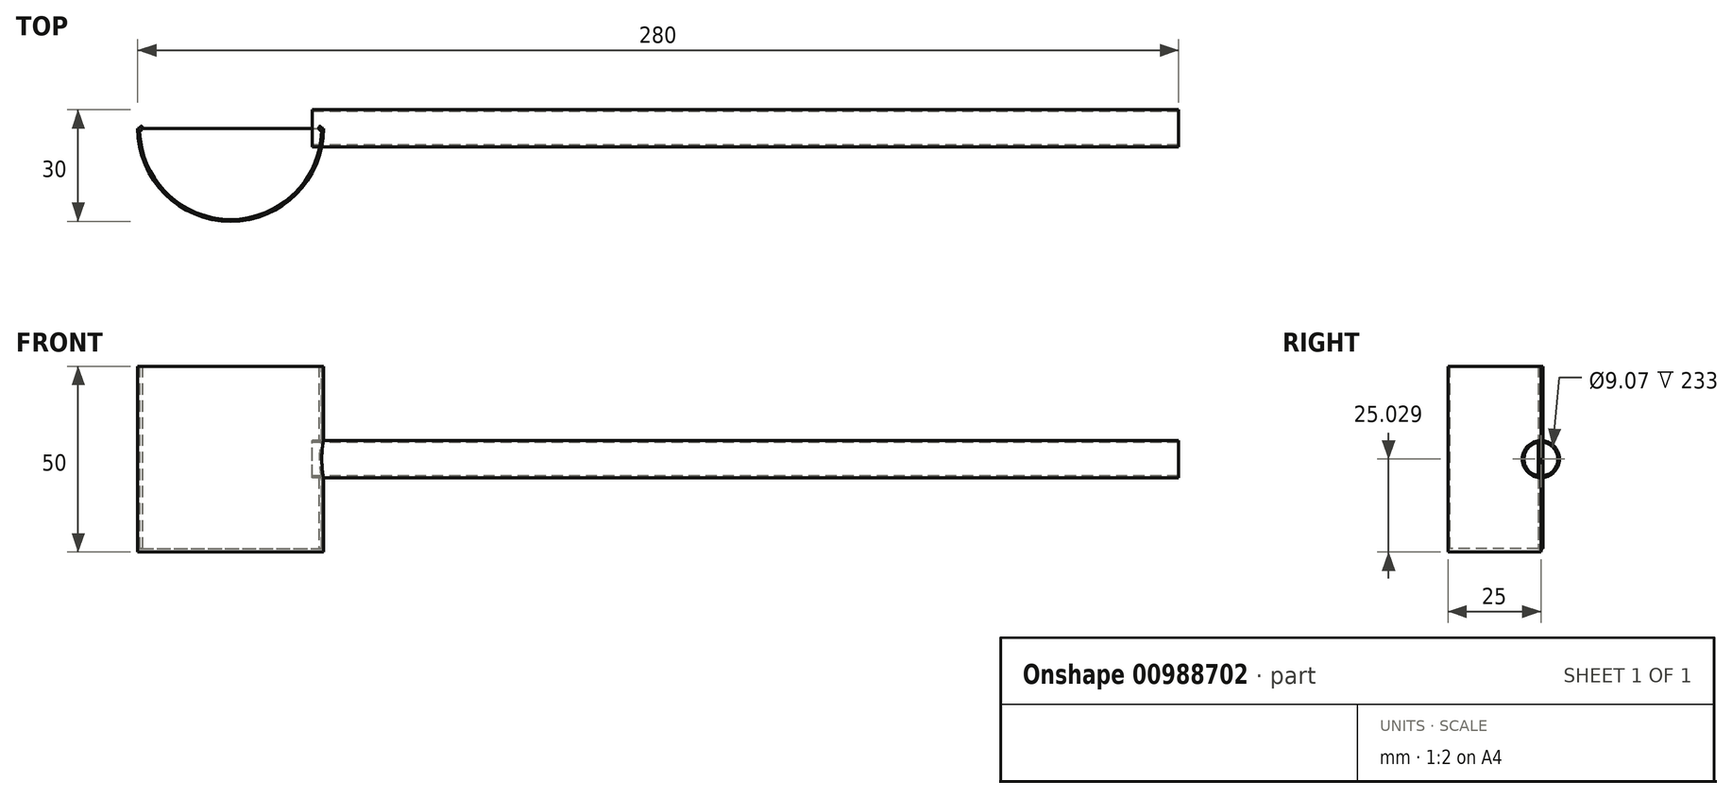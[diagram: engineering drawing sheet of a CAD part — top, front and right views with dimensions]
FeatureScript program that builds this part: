
annotation { "Feature Type Name" : "Feature", "Feature Type Description" : "" }
export const myFeature = defineFeature(function(context is Context, id is Id, definition is map)
    precondition{}
    {
        {
            var Q0;
            Q0=qCreatedBy(makeId("Top.planeOp"),FACE);
            var sketch = newSketch(context, id + "F0", { "sketchPlane" : qUnion([Q0])});
            skCircle(sketch, "E0", {"center": v(0, 0) * mm, "radius": 25 * mm});
            skSolve(sketch);
        }
        {
            var Q0;
            Q0=makeQuery(id+"F0.imprint","IMPRINT",FACE,{"disambiguationData":[TD([[makeQuery(id+"F0.imprint","IMPRINT",EDGE,{"derivedFrom":sQuery(id+"F0.wireOp",EDGE,"E0")}),1.0]])]});
            extrude(context, id + "F1", {"entities" : qUnion([Q0]), "depth" : 50 * mm, "offsetDistance" : 25 * mm});
        }
        {
            var Q0;
            Q0=makeQuery(id+"F1.opExtrude","CAP_FACE",FACE,{"disambiguationData":[OSD([sQuery(id+"F0.wireOp",EDGE,"E0")])],"isStart":false});
            var sketch = newSketch(context, id + "F2", { "sketchPlane" : qUnion([Q0])});
            skCircle(sketch, "E1", {"center": v(0, 0) * mm, "radius": 24.5 * mm});
            skSolve(sketch);
        }
        {
            var Q0;
            Q0 = qSketchRegion(id + "F2", true);
            extrude(context, id + "F3", {"entities" : qUnion([Q0]), "operationType" : NewBodyOperationType.REMOVE, "oppositeDirection" : true, "depth" : 49 * mm, "offsetDistance" : 25 * mm});
        }
        {
            var Q0;
            Q0=qCreatedBy(makeId("Front.planeOp"),FACE);
            var sketch = newSketch(context, id + "F4", { "sketchPlane" : qUnion([Q0])});
            skLineSegment(sketch, "E2.bottom", {"start": v(-75.21, -16.97) * mm, "end": v(-72.67, -16.97) * mm});
            skLineSegment(sketch, "E2.top", {"start": v(-75.21, -15.33) * mm, "end": v(-72.67, -15.33) * mm});
            skLineSegment(sketch, "E2.left", {"start": v(-75.21, -16.97) * mm, "end": v(-75.21, -15.33) * mm});
            skLineSegment(sketch, "E2.right", {"start": v(-72.67, -16.97) * mm, "end": v(-72.67, -15.33) * mm});
            skLineSegment(sketch, "E3.bottom", {"start": v(-72.67, -15.33) * mm, "end": v(60.33, -15.33) * mm});
            skLineSegment(sketch, "E3.top", {"start": v(-72.67, 64.87) * mm, "end": v(60.33, 64.87) * mm});
            skLineSegment(sketch, "E3.left", {"start": v(-72.67, -15.33) * mm, "end": v(-72.67, 64.87) * mm});
            skLineSegment(sketch, "E3.right", {"start": v(60.33, -15.33) * mm, "end": v(60.33, 64.87) * mm});
            skSolve(sketch);
        }
        {
            var Q0;
            Q0=makeQuery(id+"F4.imprint","IMPRINT",FACE,{"disambiguationData":[TD([[makeQuery(id+"F4.imprint","IMPRINT",EDGE,{"derivedFrom":sQuery(id+"F4.wireOp",EDGE,"E3.bottom")}),1.0]])]});
            extrude(context, id + "F5", {"entities" : qUnion([Q0]), "operationType" : NewBodyOperationType.REMOVE, "oppositeDirection" : true, "depth" : 25 * mm, "offsetDistance" : 25 * mm});
        }
        {
            var Q0;
            Q0=makeQuery(id+"F3.boolean.opBoolean","COPY",FACE,{"derivedFrom":makeQuery(id+"F3.opExtrude","CAP_FACE",FACE,{"disambiguationData":[OSD([sQuery(id+"F2.wireOp",EDGE,"E1")])],"isStart":false})});
            var sketch = newSketch(context, id + "F6", { "sketchPlane" : qUnion([Q0])});
            skCircle(sketch, "E4", {"center": v(-24.03, 0.3) * mm, "radius": 0.25 * mm});
            skCircle(sketch, "E5", {"center": v(-24.5, 0) * mm, "radius": 0.73 * mm});
            skLineSegment(sketch, "E6", {"start": v(-23.77, 0) * mm, "end": v(-23.78, 0.32) * mm});
            skLineSegment(sketch, "E7", {"start": v(-24.5, 0) * mm, "end": v(-24.25, 0.43) * mm});
            skSolve(sketch);
        }
        {
            var Q0;
            {var subQ0=sQuery(id+"F6.wireOp",EDGE,"E4");var subQ1=makeQuery(id+"F6.imprint","INTERSECT",VERTEX,{"derivedFrom":[subQ0,sQuery(id+"F6.wireOp",EDGE,"E7")]});Q0=makeQuery(id+"F6.imprint","IMPRINT",FACE,{"disambiguationData":[TD([[makeQuery(id+"F6.imprint","IMPRINT",EDGE,{"disambiguationData":[TD([[subQ1,1.0]])],"derivedFrom":subQ0}),1.0]])]});}
            var Q1;
            {var subQ0=sQuery(id+"F6.wireOp",EDGE,"E4");var subQ1=makeQuery(id+"F6.imprint","INTERSECT",VERTEX,{"derivedFrom":[subQ0,sQuery(id+"F6.wireOp",EDGE,"E6")]});Q1=makeQuery(id+"F6.imprint","IMPRINT",FACE,{"disambiguationData":[TD([[makeQuery(id+"F6.imprint","IMPRINT",EDGE,{"disambiguationData":[TD([[subQ1,-1.0]])],"derivedFrom":subQ0}),1.0]])]});}
            var Q2;
            {var subQ0=sQuery(id+"F6.wireOp",EDGE,"E7");Q2=makeQuery(id+"F6.imprint","IMPRINT",FACE,{"disambiguationData":[TD([[makeQuery(id+"F6.imprint","IMPRINT",EDGE,{"derivedFrom":subQ0}),-1.0]])]});}
            var Q3;
            {var subQ0=sQuery(id+"F6.wireOp",EDGE,"E6");var subQ1=sQuery(id+"F6.wireOp",EDGE,"E4");var subQ2=makeQuery(id+"F6.imprint","INTERSECT",VERTEX,{"derivedFrom":[subQ1,subQ0]});Q3=makeQuery(id+"F6.imprint","IMPRINT",FACE,{"disambiguationData":[TD([[makeQuery(id+"F6.imprint","IMPRINT",EDGE,{"disambiguationData":[TD([[subQ2,1.0]])],"derivedFrom":subQ1}),-1.0]])]});}
            var Q4;
            {var subQ0=sQuery(id+"F6.wireOp",EDGE,"E5");var subQ1=sQuery(id+"F2.wireOp",EDGE,"E1");var subQ4=makeQuery(id+"F3.boolean.opBoolean","COPY",EDGE,{"derivedFrom":makeQuery(id+"F3.opExtrude","CAP_EDGE",EDGE,{"disambiguationData":[OSD([subQ1])],"isStart":false})});var subQ5=makeQuery(id+"F6.imprint","INTERSECT",VERTEX,{"derivedFrom":[subQ4,subQ0]});Q4=makeQuery(id+"F6.imprint","IMPRINT",FACE,{"disambiguationData":[TD([[makeQuery(id+"F6.imprint","IMPRINT",EDGE,{"disambiguationData":[TD([[subQ5,-1.0]])],"derivedFrom":subQ0}),1.0]])]});}
            extrude(context, id + "F7", {"entities" : qUnion([Q0, Q1, Q2, Q3, Q4]), "operationType" : NewBodyOperationType.ADD, "depth" : 49 * mm, "offsetDistance" : 25 * mm});
        }
        {
            var Q0;
            Q0=qCreatedBy(makeId("Right.planeOp"),FACE);
            var sketch = newSketch(context, id + "F8", { "sketchPlane" : qUnion([Q0])});
            skLineSegment(sketch, "E8.bottom", {"start": v(-56.16, -10.43) * mm, "end": v(34.75, -10.43) * mm});
            skLineSegment(sketch, "E8.top", {"start": v(-56.16, 66.5) * mm, "end": v(34.75, 66.5) * mm});
            skLineSegment(sketch, "E8.left", {"start": v(-56.16, -10.43) * mm, "end": v(-56.16, 66.5) * mm});
            skLineSegment(sketch, "E8.right", {"start": v(34.75, -10.43) * mm, "end": v(34.75, 66.5) * mm});
            skSolve(sketch);
        }
        {
            var Q0;
            Q0=makeQuery(id+"F8.imprint","IMPRINT",FACE,{"disambiguationData":[TD([[makeQuery(id+"F8.imprint","IMPRINT",EDGE,{"derivedFrom":sQuery(id+"F8.wireOp",EDGE,"E8.bottom")}),1.0]])]});
            extrude(context, id + "F9", {"entities" : qUnion([Q0]), "operationType" : NewBodyOperationType.REMOVE, "depth" : 25 * mm, "offsetDistance" : 25 * mm});
        }
        {
            var Q0;
            Q0=makeQuery(id+"F1.opExtrude","SWEPT_BODY",BODY,{"disambiguationData":[OSD([sQuery(id+"F0.wireOp",EDGE,"E0")])]});
            var Q1;
            Q1=makeQuery(id+"F9.boolean.opBoolean","COPY",FACE,{"derivedFrom":makeQuery(id+"F9.opExtrude","CAP_FACE",FACE,{"disambiguationData":[OSD([sQuery(id+"F8.wireOp",EDGE,"E8.bottom"),sQuery(id+"F8.wireOp",EDGE,"E8.top"),sQuery(id+"F8.wireOp",EDGE,"E8.left"),sQuery(id+"F8.wireOp",EDGE,"E8.right")])],"isStart":true})});
            mirror(context, id + "F10", {"operationType" : NewBodyOperationType.ADD, "entities" : qUnion([Q0]), "mirrorPlane" : qUnion([Q1])});
        }
        {
            var Q0;
            Q0=qCreatedBy(makeId("Right.planeOp"),FACE);
            var sketch = newSketch(context, id + "F11", { "sketchPlane" : qUnion([Q0])});
            skCircle(sketch, "E9", {"center": v(0, 25.03) * mm, "radius": 5 * mm});
            skCircle(sketch, "E10", {"center": v(0, 25.03) * mm, "radius": 4.5 * mm});
            skSolve(sketch);
        }
        {
            var Q0;
            Q0 = qSketchRegion(id + "F11", true);
            extrude(context, id + "F12", {"entities" : qUnion([Q0]), "operationType" : NewBodyOperationType.ADD, "depth" : 255 * mm, "offsetDistance" : 25 * mm});
        }
        {
            var Q0;
            Q0 = qSketchRegion(id + "F11", true);
            extrude(context, id + "F13", {"entities" : qUnion([Q0]), "operationType" : NewBodyOperationType.REMOVE, "depth" : 22 * mm, "offsetDistance" : 25 * mm});
        }
        {
            var Q0;
            Q0=qCreatedBy(makeId("Right.planeOp"),FACE);
            var sketch = newSketch(context, id + "F14", { "sketchPlane" : qUnion([Q0])});
            skCircle(sketch, "E11", {"center": v(0, 25.03) * mm, "radius": 4.54 * mm});
            skSolve(sketch);
        }
        {
            var Q0;
            Q0=makeQuery(id+"F14.imprint","IMPRINT",FACE,{"disambiguationData":[TD([[makeQuery(id+"F14.imprint","IMPRINT",EDGE,{"derivedFrom":sQuery(id+"F14.wireOp",EDGE,"E11")}),1.0]])]});
            extrude(context, id + "F15", {"entities" : qUnion([Q0]), "operationType" : NewBodyOperationType.REMOVE, "depth" : 500 * mm, "offsetDistance" : 25 * mm});
        }
    });
